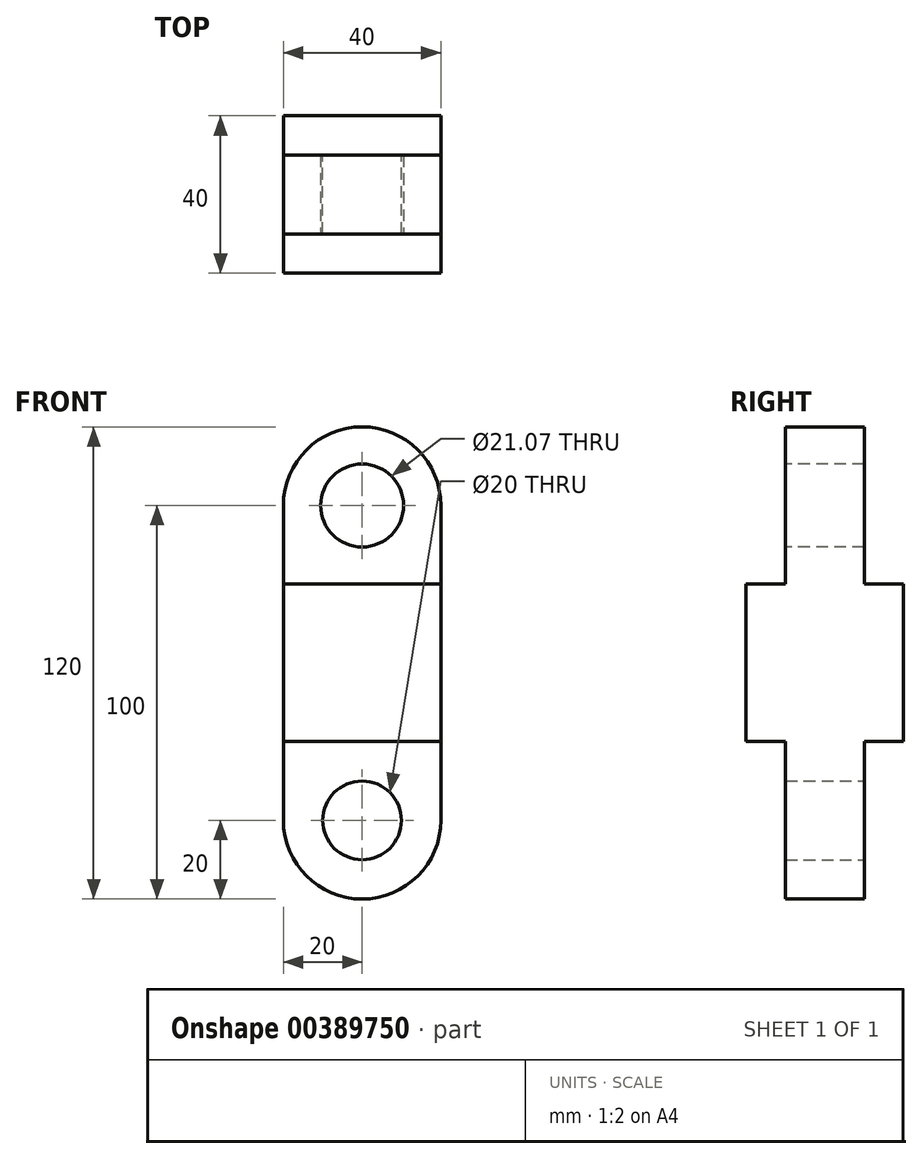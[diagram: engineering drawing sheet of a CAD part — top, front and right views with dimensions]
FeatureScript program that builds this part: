
annotation { "Feature Type Name" : "Feature", "Feature Type Description" : "" }
export const myFeature = defineFeature(function(context is Context, id is Id, definition is map)
    precondition{}
    {
        {
            var Q0;
            Q0=qCreatedBy(makeId("Front.planeOp"),FACE);
            var sketch = newSketch(context, id + "F0", { "sketchPlane" : qUnion([Q0])});
            skLineSegment(sketch, "E0.bottom", {"start": v(20, -60) * mm, "end": v(-20, -60) * mm});
            skLineSegment(sketch, "E0.top", {"start": v(20, 60) * mm, "end": v(-20, 60) * mm});
            skLineSegment(sketch, "E0.left", {"start": v(20, -60) * mm, "end": v(20, 60) * mm});
            skLineSegment(sketch, "E0.right", {"start": v(-20, -60) * mm, "end": v(-20, 60) * mm});
            skPoint(sketch, "E0.middle", {"position": v(0, 0) * mm});
            skSolve(sketch);
        }
        {
            var Q0;
            Q0 = qSketchRegion(id + "F0", true);
            extrude(context, id + "F1", {"entities" : qUnion([Q0]), "depth" : 10 * mm});
        }
        {
            var Q0;
            Q0=makeQuery(id+"F1.opExtrude","CAP_FACE",FACE,{"disambiguationData":[OSD([sQuery(id+"F0.wireOp",EDGE,"E0.bottom"),sQuery(id+"F0.wireOp",EDGE,"E0.top"),sQuery(id+"F0.wireOp",EDGE,"E0.left"),sQuery(id+"F0.wireOp",EDGE,"E0.right")])],"isStart":false});
            var sketch = newSketch(context, id + "F2", { "sketchPlane" : qUnion([Q0])});
            skLineSegment(sketch, "E1.bottom", {"start": v(20, -20) * mm, "end": v(-20, -20) * mm});
            skLineSegment(sketch, "E1.top", {"start": v(20, 20) * mm, "end": v(-20, 20) * mm});
            skLineSegment(sketch, "E1.left", {"start": v(20, -20) * mm, "end": v(20, 20) * mm});
            skLineSegment(sketch, "E1.right", {"start": v(-20, -20) * mm, "end": v(-20, 20) * mm});
            skPoint(sketch, "E1.middle", {"position": v(0, 0) * mm});
            skSolve(sketch);
        }
        {
            var Q0;
            Q0 = qSketchRegion(id + "F2", true);
            extrude(context, id + "F3", {"entities" : qUnion([Q0]), "operationType" : NewBodyOperationType.ADD, "depth" : 10 * mm});
        }
        {
            var Q0;
            Q0=makeQuery(id+"F1.opExtrude","SWEPT_BODY",BODY,{"disambiguationData":[OSD([sQuery(id+"F0.wireOp",EDGE,"E0.bottom"),sQuery(id+"F0.wireOp",EDGE,"E0.top"),sQuery(id+"F0.wireOp",EDGE,"E0.left"),sQuery(id+"F0.wireOp",EDGE,"E0.right")])]});
            var Q1;
            Q1=makeQuery(id+"F1.opExtrude","CAP_FACE",FACE,{"disambiguationData":[OSD([sQuery(id+"F0.wireOp",EDGE,"E0.bottom"),sQuery(id+"F0.wireOp",EDGE,"E0.top"),sQuery(id+"F0.wireOp",EDGE,"E0.left"),sQuery(id+"F0.wireOp",EDGE,"E0.right")])],"isStart":true});
            mirror(context, id + "F4", {"operationType" : NewBodyOperationType.ADD, "entities" : qUnion([Q0]), "mirrorPlane" : qUnion([Q1])});
        }
        {
            var Q0;
            {var subQ0=sQuery(id+"F0.wireOp",EDGE,"E0.left");var subQ1=sQuery(id+"F0.wireOp",EDGE,"E0.right");var subQ2=sQuery(id+"F0.wireOp",EDGE,"E0.top");Q0=makeQuery(id+"F3.boolean.opBoolean","SPLIT",FACE,{"disambiguationData":[TD([makeQuery(id+"F1.opExtrude","SWEPT_FACE",FACE,{"disambiguationData":[OSD([subQ2])]})])],"derivedFrom":makeQuery(id+"F1.opExtrude","CAP_FACE",FACE,{"disambiguationData":[OSD([sQuery(id+"F0.wireOp",EDGE,"E0.bottom"),subQ2,subQ0,subQ1])],"isStart":false})});}
            var sketch = newSketch(context, id + "F5", { "sketchPlane" : qUnion([Q0])});
            skCircle(sketch, "E2", {"center": v(0, 40) * mm, "radius": 10.54 * mm});
            skSolve(sketch);
        }
        {
            var Q0;
            Q0 = qSketchRegion(id + "F5", true);
            var Q1;
            {var subQ0=sQuery(id+"F0.wireOp",EDGE,"E0.left");var subQ1=sQuery(id+"F0.wireOp",EDGE,"E0.right");var subQ2=sQuery(id+"F0.wireOp",EDGE,"E0.top");Q1=makeQuery(id+"F4.opPattern","COPY",FACE,{"derivedFrom":makeQuery(id+"F3.boolean.opBoolean","SPLIT",FACE,{"disambiguationData":[TD([makeQuery(id+"F1.opExtrude","SWEPT_FACE",FACE,{"disambiguationData":[OSD([subQ2])]})])],"derivedFrom":makeQuery(id+"F1.opExtrude","CAP_FACE",FACE,{"disambiguationData":[OSD([sQuery(id+"F0.wireOp",EDGE,"E0.bottom"),subQ2,subQ0,subQ1])],"isStart":false})}),"instanceName":"1"});}
            extrude(context, id + "F6", {"entities" : qUnion([Q0]), "operationType" : NewBodyOperationType.REMOVE, "endBound" : BoundingType.UP_TO_SURFACE, "oppositeDirection" : true, "endBoundEntityFace" : qUnion([Q1]), "depth" : 25 * mm});
        }
        {
            var Q0;
            {var subQ0=sQuery(id+"F0.wireOp",EDGE,"E0.left");var subQ1=sQuery(id+"F0.wireOp",EDGE,"E0.right");var subQ2=sQuery(id+"F0.wireOp",EDGE,"E0.bottom");Q0=makeQuery(id+"F4.opPattern","COPY",FACE,{"derivedFrom":makeQuery(id+"F3.boolean.opBoolean","SPLIT",FACE,{"disambiguationData":[TD([makeQuery(id+"F1.opExtrude","SWEPT_FACE",FACE,{"disambiguationData":[OSD([subQ2])]})])],"derivedFrom":makeQuery(id+"F1.opExtrude","CAP_FACE",FACE,{"disambiguationData":[OSD([subQ2,sQuery(id+"F0.wireOp",EDGE,"E0.top"),subQ0,subQ1])],"isStart":false})}),"instanceName":"1"});}
            var sketch = newSketch(context, id + "F7", { "sketchPlane" : qUnion([Q0])});
            skCircle(sketch, "E3", {"center": v(0, -40) * mm, "radius": 10 * mm});
            skSolve(sketch);
        }
        {
            var Q0;
            Q0 = qSketchRegion(id + "F7", true);
            var Q1;
            {var subQ0=sQuery(id+"F0.wireOp",EDGE,"E0.left");var subQ1=sQuery(id+"F0.wireOp",EDGE,"E0.right");var subQ2=sQuery(id+"F0.wireOp",EDGE,"E0.bottom");Q1=makeQuery(id+"F3.boolean.opBoolean","SPLIT",FACE,{"disambiguationData":[TD([makeQuery(id+"F1.opExtrude","SWEPT_FACE",FACE,{"disambiguationData":[OSD([subQ2])]})])],"derivedFrom":makeQuery(id+"F1.opExtrude","CAP_FACE",FACE,{"disambiguationData":[OSD([subQ2,sQuery(id+"F0.wireOp",EDGE,"E0.top"),subQ0,subQ1])],"isStart":false})});}
            extrude(context, id + "F8", {"entities" : qUnion([Q0]), "operationType" : NewBodyOperationType.REMOVE, "endBound" : BoundingType.UP_TO_SURFACE, "oppositeDirection" : true, "endBoundEntityFace" : qUnion([Q1]), "depth" : 25 * mm});
        }
        {
            var Q0;
            {var subQ0=makeQuery(id+"F1.opExtrude","SWEPT_EDGE",EDGE,{"disambiguationData":[OSD([sQuery(id+"F0.wireOp",EDGE,"E0.top"),sQuery(id+"F0.wireOp",EDGE,"E0.right")])]});Q0=makeQuery(id+"F4.boolean.opBoolean","MERGE",EDGE,{"derivedFrom":[subQ0,makeQuery(id+"F4.opPattern","COPY",EDGE,{"derivedFrom":subQ0,"instanceName":"1"})]});}
            var Q1;
            {var subQ0=makeQuery(id+"F1.opExtrude","SWEPT_EDGE",EDGE,{"disambiguationData":[OSD([sQuery(id+"F0.wireOp",EDGE,"E0.top"),sQuery(id+"F0.wireOp",EDGE,"E0.left")])]});Q1=makeQuery(id+"F4.boolean.opBoolean","MERGE",EDGE,{"derivedFrom":[subQ0,makeQuery(id+"F4.opPattern","COPY",EDGE,{"derivedFrom":subQ0,"instanceName":"1"})]});}
            fillet(context, id + "F9", {"entities" : qUnion([Q0, Q1]), "radius" : 20 * mm, "tangentPropagation" : true, "allowEdgeOverflow" : false});
        }
        {
            var Q0;
            {var subQ0=makeQuery(id+"F1.opExtrude","SWEPT_EDGE",EDGE,{"disambiguationData":[OSD([sQuery(id+"F0.wireOp",EDGE,"E0.bottom"),sQuery(id+"F0.wireOp",EDGE,"E0.left")])]});Q0=makeQuery(id+"F4.boolean.opBoolean","MERGE",EDGE,{"derivedFrom":[subQ0,makeQuery(id+"F4.opPattern","COPY",EDGE,{"derivedFrom":subQ0,"instanceName":"1"})]});}
            var Q1;
            {var subQ0=makeQuery(id+"F1.opExtrude","SWEPT_EDGE",EDGE,{"disambiguationData":[OSD([sQuery(id+"F0.wireOp",EDGE,"E0.bottom"),sQuery(id+"F0.wireOp",EDGE,"E0.right")])]});Q1=makeQuery(id+"F4.boolean.opBoolean","MERGE",EDGE,{"derivedFrom":[subQ0,makeQuery(id+"F4.opPattern","COPY",EDGE,{"derivedFrom":subQ0,"instanceName":"1"})]});}
            fillet(context, id + "F10", {"entities" : qUnion([Q0, Q1]), "radius" : 20 * mm, "tangentPropagation" : true, "allowEdgeOverflow" : false});
        }
    });
